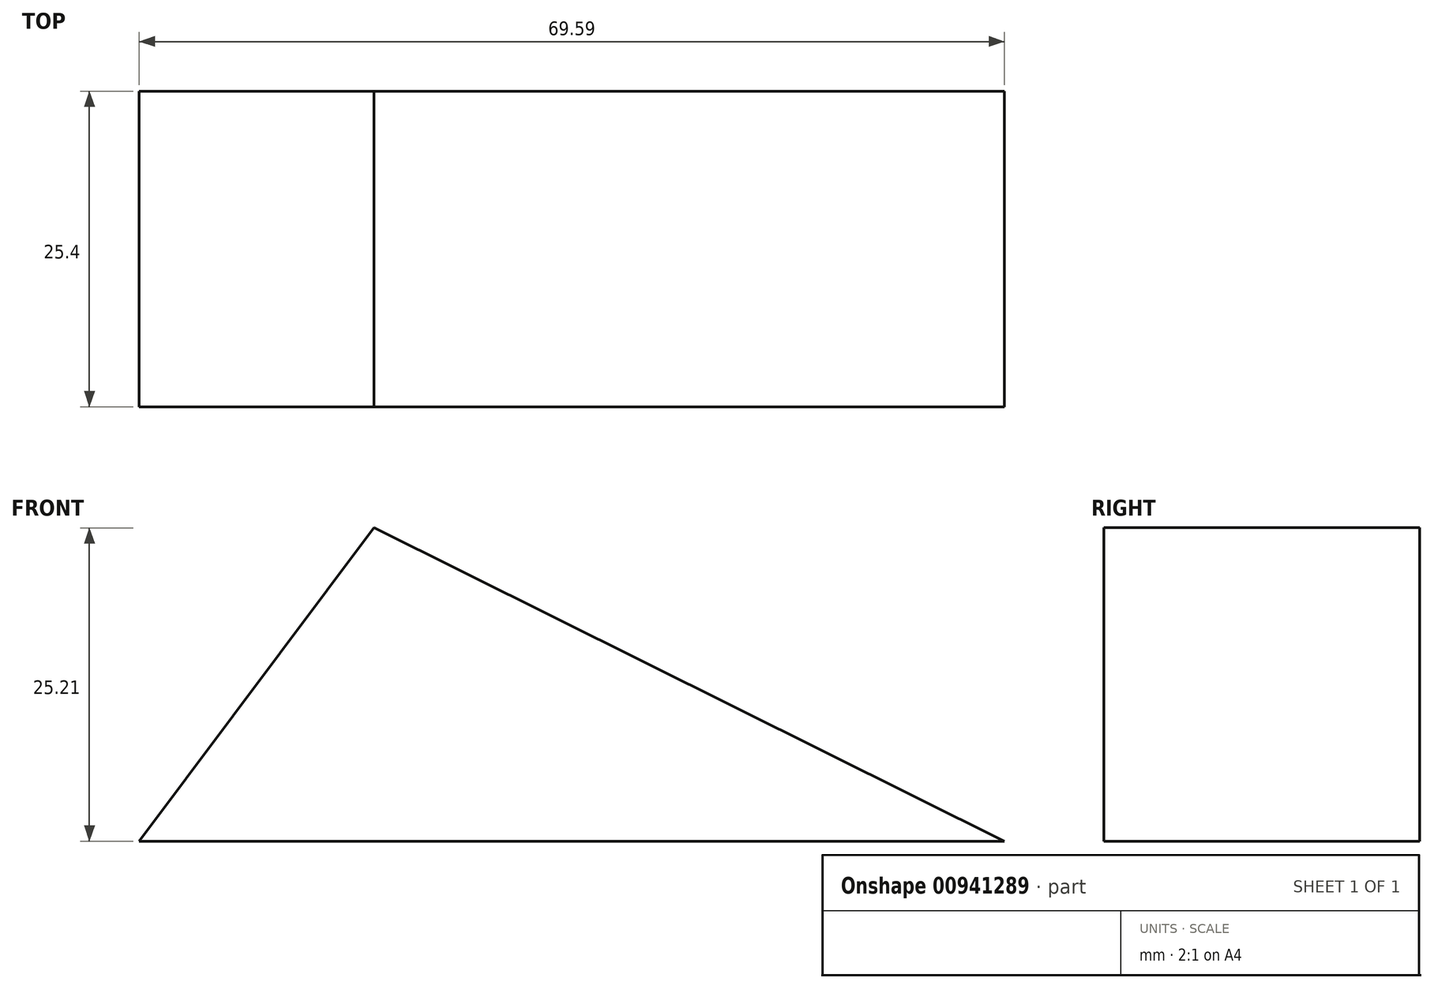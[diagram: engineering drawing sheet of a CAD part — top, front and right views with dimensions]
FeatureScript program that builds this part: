
annotation { "Feature Type Name" : "Feature", "Feature Type Description" : "" }
export const myFeature = defineFeature(function(context is Context, id is Id, definition is map)
    precondition{}
    {
        {
            var Q0;
            Q0=qCreatedBy(makeId("Front.planeOp"),FACE);
            var sketch = newSketch(context, id + "F0", { "sketchPlane" : qUnion([Q0])});
            skLineSegment(sketch, "E0", {"start": v(35.92, 0) * mm, "end": v(-33.67, 0) * mm});
            skLineSegment(sketch, "E1", {"start": v(-33.67, 0) * mm, "end": v(-14.8, 25.21) * mm});
            skLineSegment(sketch, "E2", {"start": v(-14.8, 25.21) * mm, "end": v(35.92, 0) * mm});
            skSolve(sketch);
        }
        {
            var Q0;
            Q0=makeQuery(id+"F0.imprint","IMPRINT",FACE,{"disambiguationData":[TD([[makeQuery(id+"F0.imprint","IMPRINT",EDGE,{"derivedFrom":sQuery(id+"F0.wireOp",EDGE,"E0")}),-1.0]])]});
            extrude(context, id + "F1", {"entities" : qUnion([Q0]), "depth" : 25.4 * mm, "offsetDistance" : 25.4 * mm});
        }
    });
